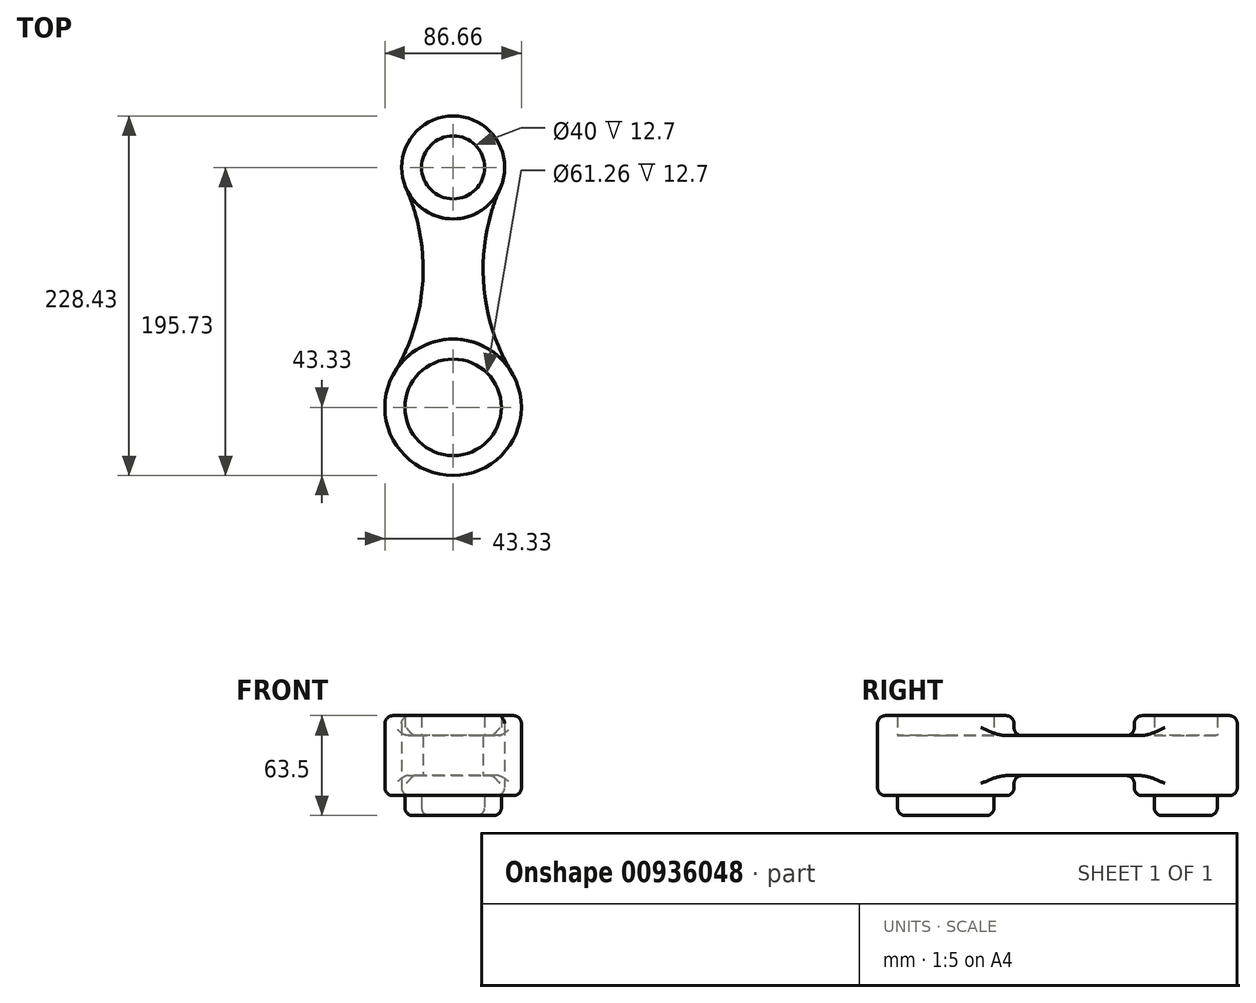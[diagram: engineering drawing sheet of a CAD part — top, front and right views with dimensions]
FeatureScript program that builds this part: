
annotation { "Feature Type Name" : "Feature", "Feature Type Description" : "" }
export const myFeature = defineFeature(function(context is Context, id is Id, definition is map)
    precondition{}
    {
        {
            var Q0;
            Q0=qCreatedBy(makeId("Top.planeOp"),FACE);
            var sketch = newSketch(context, id + "F0", { "sketchPlane" : qUnion([Q0])});
            skLineSegment(sketch, "E0", {"start": v(0, 0) * mm, "end": v(0, -152.4) * mm, "construction": true});
            skCircle(sketch, "E1", {"center": v(0, 0) * mm, "radius": 20 * mm});
            skCircle(sketch, "E2", {"center": v(0, 0) * mm, "radius": 32.7 * mm});
            skCircle(sketch, "E3", {"center": v(0, -152.4) * mm, "radius": 30.63 * mm});
            skCircle(sketch, "E4", {"center": v(0, -152.4) * mm, "radius": 43.33 * mm});
            skArc(sketch, "E5", {"start": v(29.9, -13.25) * mm, "mid": v(19.26, -72.55) * mm, "end": v(37.15, -130.09) * mm});
            skArc(sketch, "E6.MirrorCS", {"start": v(-29.9, -13.25) * mm, "mid": v(-19.26, -72.55) * mm, "end": v(-37.15, -130.09) * mm});
            skSolve(sketch);
        }
        {
            var Q0;
            {var subQ0=sQuery(id+"F0.wireOp",EDGE,"E5");Q0=makeQuery(id+"F0.imprint","IMPRINT",FACE,{"disambiguationData":[TD([[makeQuery(id+"F0.imprint","IMPRINT",EDGE,{"derivedFrom":subQ0}),-1.0]])]});}
            extrude(context, id + "F1", {"entities" : qUnion([Q0]), "endBound" : BoundingType.SYMMETRIC, "depth" : 25.4 * mm, "offsetDistance" : 25.4 * mm});
        }
        {
            var Q0;
            Q0=makeQuery(id+"F0.imprint","IMPRINT",FACE,{"disambiguationData":[TD([[makeQuery(id+"F0.imprint","IMPRINT",EDGE,{"derivedFrom":sQuery(id+"F0.wireOp",EDGE,"E1")}),-1.0]])]});
            var Q1;
            Q1=makeQuery(id+"F0.imprint","IMPRINT",FACE,{"disambiguationData":[TD([[makeQuery(id+"F0.imprint","IMPRINT",EDGE,{"derivedFrom":sQuery(id+"F0.wireOp",EDGE,"E3")}),-1.0]])]});
            extrude(context, id + "F2", {"entities" : qUnion([Q0, Q1]), "operationType" : NewBodyOperationType.ADD, "endBound" : BoundingType.SYMMETRIC, "depth" : 50.8 * mm, "offsetDistance" : 25.4 * mm});
        }
        {
            var Q0;
            Q0=makeQuery(id+"F0.imprint","IMPRINT",FACE,{"disambiguationData":[TD([[makeQuery(id+"F0.imprint","IMPRINT",EDGE,{"derivedFrom":sQuery(id+"F0.wireOp",EDGE,"E1")}),1.0]])]});
            var Q1;
            Q1=makeQuery(id+"F0.imprint","IMPRINT",FACE,{"disambiguationData":[TD([[makeQuery(id+"F0.imprint","IMPRINT",EDGE,{"derivedFrom":sQuery(id+"F0.wireOp",EDGE,"E3")}),1.0]])]});
            extrude(context, id + "F3", {"entities" : qUnion([Q0, Q1]), "operationType" : NewBodyOperationType.ADD, "depth" : 12.7 * mm, "offsetDistance" : 25.4 * mm, "hasSecondDirection" : true, "secondDirectionOppositeDirection" : true, "secondDirectionDepth" : 38.1 * mm});
        }
        {
            var Q0;
            Q0=makeQuery(id+"F2.opExtrude","SWEPT_FACE",FACE,{"disambiguationData":[OSD([sQuery(id+"F0.wireOp",EDGE,"E2")])]});
            var Q1;
            Q1=makeQuery(id+"F2.opExtrude","SWEPT_FACE",FACE,{"disambiguationData":[OSD([sQuery(id+"F0.wireOp",EDGE,"E4")])]});
            var Q2;
            Q2=makeQuery(id+"F3.opExtrude","CAP_EDGE",EDGE,{"disambiguationData":[OSD([sQuery(id+"F0.wireOp",EDGE,"E1")])],"isStart":true});
            var Q3;
            Q3=makeQuery(id+"F3.opExtrude","CAP_EDGE",EDGE,{"disambiguationData":[OSD([sQuery(id+"F0.wireOp",EDGE,"E3")])],"isStart":true});
            fillet(context, id + "F4", {"entities" : qUnion([Q0, Q1, Q2, Q3]), "radius" : 5.08 * mm, "tangentPropagation" : true, "allowEdgeOverflow" : false});
        }
    });
